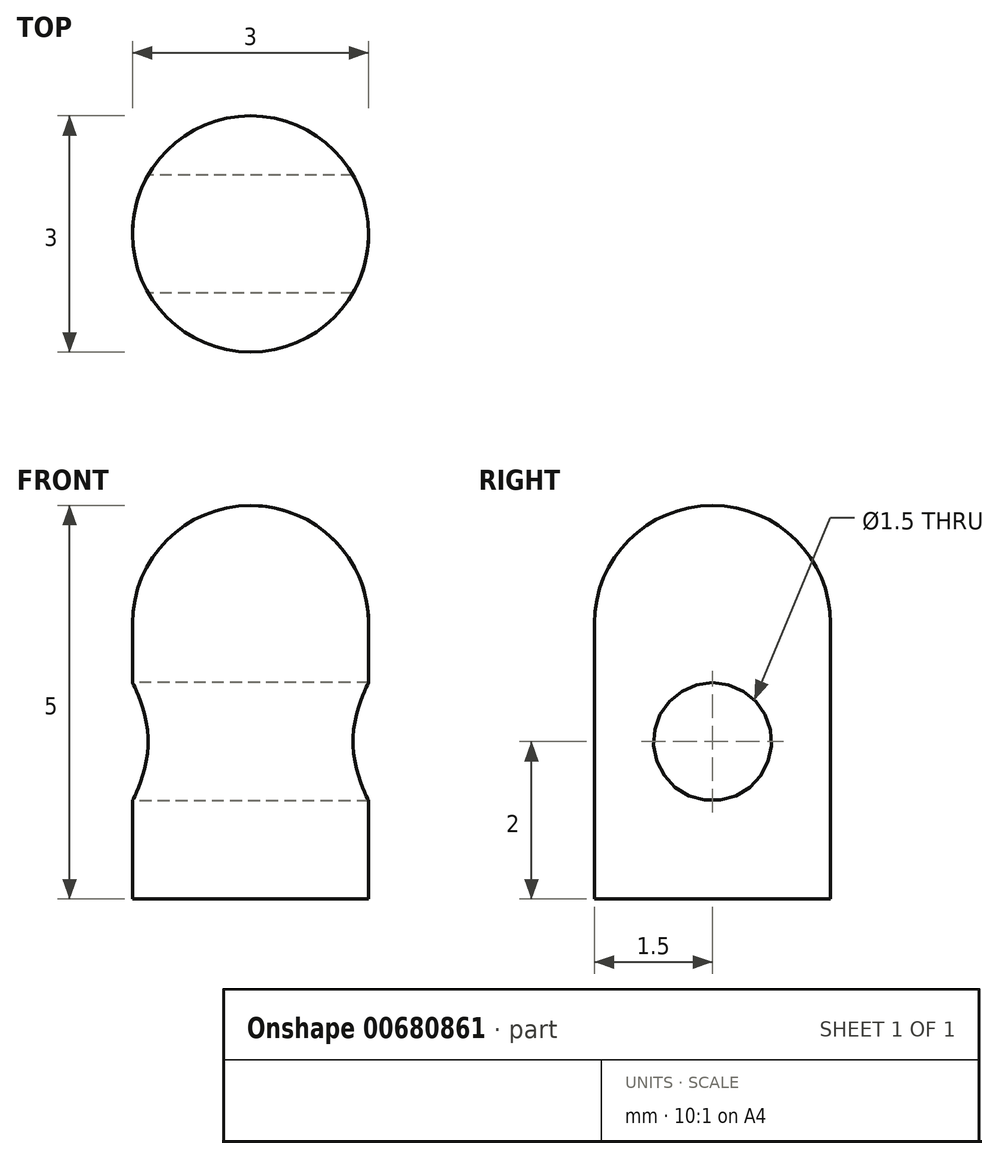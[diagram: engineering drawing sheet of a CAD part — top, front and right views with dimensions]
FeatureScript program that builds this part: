
annotation { "Feature Type Name" : "Feature", "Feature Type Description" : "" }
export const myFeature = defineFeature(function(context is Context, id is Id, definition is map)
    precondition{}
    {
        {
            var Q0;
            Q0=qCreatedBy(makeId("Top.planeOp"),FACE);
            var sketch = newSketch(context, id + "F0", { "sketchPlane" : qUnion([Q0])});
            skCircle(sketch, "E0", {"center": v(0, 0) * mm, "radius": 1.5 * mm});
            skSolve(sketch);
        }
        {
            var Q0;
            Q0=makeQuery(id+"F0.imprint","IMPRINT",FACE,{"disambiguationData":[TD([[makeQuery(id+"F0.imprint","IMPRINT",EDGE,{"derivedFrom":sQuery(id+"F0.wireOp",EDGE,"E0")}),1.0]])]});
            extrude(context, id + "F1", {"entities" : qUnion([Q0]), "depth" : 5 * mm, "offsetDistance" : 25 * mm});
        }
        {
            var Q0;
            Q0=makeQuery(id+"F1.opExtrude","CAP_FACE",FACE,{"disambiguationData":[OSD([sQuery(id+"F0.wireOp",EDGE,"E0")])],"isStart":false});
            fillet(context, id + "F2", {"entities" : qUnion([Q0]), "radius" : 1.5 * mm, "tangentPropagation" : true, "allowEdgeOverflow" : false});
        }
        {
            var Q0;
            Q0=qCreatedBy(makeId("Right.planeOp"),FACE);
            var sketch = newSketch(context, id + "F3", { "sketchPlane" : qUnion([Q0])});
            skCircle(sketch, "E1", {"center": v(0, 2) * mm, "radius": 0.75 * mm});
            skSolve(sketch);
        }
        {
            var Q0;
            Q0 = qSketchRegion(id + "F3", true);
            extrude(context, id + "F4", {"entities" : qUnion([Q0]), "operationType" : NewBodyOperationType.REMOVE, "depth" : 3 * mm, "offsetDistance" : 25 * mm, "symmetric" : true});
        }
    });
